# Revit family: 70740X0
name_source: partatom
category: Plumbing Fixtures
revit_build: Autodesk Revit 2018 (Build: 20170223_1515(x64)
units: mm (PartAtom-declared; Revit-internal decimal feet)

## family parameters
Always vertical = No
Cut with Voids When Loaded = No
OmniClass Number = 23.45.55.14
OmniClass Title = Single Faucets
Part Type = Normal
Room Calculation Point = No
Round Connector Dimension = Use Diameter
Shared = Yes
Work Plane-Based = Yes

## types (6) — shared parameters
ADA Compliant = Yes
Assembly Code = D2020300
CEC Compliant = Yes
CW Connection = No
CWFU = 1.5
CalGreen Compliant = Yes
Default Elevation = 0"
Flow Rate = 1.5 GPM (5.7L/min)
HW Connection = No
HWFU = 1.5
Height = 6 1/2"
Installation Type = Deck Mounted
Length = 10 3/8"
Length 2 = 9 1/8"
Manufacturer = American Standard
Product Documentation Link = https://americanstandard.box.com
Product Page URL = https://www.americanstandard-us.com
Revised Date = 08/13/2022
Tempered Water Connection = Yes
Tempered Water Connection Diameter = 3/8"
URL = http://www.americanstandard-us.com
Vent Connection = No
Warranty Information = Limited lifetime warranty
Waste Connection = No
Width = 8 1/2"
zero-valued in all types: WFU

## per-type parameters (varying)
| type | Deck Plate | Description | Finish | Material | Mounting Height Faucet | Side-Spray | Width 2 |
| 7074000.002 | Yes | Colony® PRO Single-Handle Kitchen Faucet 1.5 gpm/5.7 L/min | Brass-American Standard-002-Polished Chrome | Brass-American Standard-002-Polished Chrome | 3/8" | Yes | 8" |
| 7074010.002 | No | Colony® PRO Single-Handle Kitchen Faucet 1.5 gpm/5.7 L/min | Brass-American Standard-002-Polished Chrome | Brass-American Standard-002-Polished Chrome | 0" | No | 8" |
| 7074030.002 | Yes | Colony® PRO Single-Handle Kitchen Faucet 1.5 gpm/5.7 L/min With Side Spray | Brass-American Standard-002-Polished Chrome | Brass-American Standard-002-Polished Chrome | 3/8" | Yes | 3" |
| 7074040.002 | Yes | Colony® PRO Single-Handle Kitchen Faucet 1.5 gpm/5.7 L/min With Side Spray | Brass-American Standard-002-Polished Chrome | Brass-American Standard-002-Polished Chrome | 3/8" | Yes | 8" |
| 7074000.075 | Yes | Colony® PRO Single-Handle Kitchen Faucet 1.5 gpm/5.7 L/min | Brass-American Standard-075-Stainless Steel | Brass-American Standard-075-Stainless Steel | 3/8" | Yes | 8" |
| 7074040.075 | Yes | Colony® PRO Single-Handle Kitchen Faucet 1.5 gpm/5.7 L/min With Side Spray | Brass-American Standard-075-Stainless Steel | Brass-American Standard-075-Stainless Steel | 3/8" | Yes | 8" |

note: column(s) folded — value = type name in every type: Model

## geometry (parser evidence)
native form markers: Sweep x6
no freeform markers — native parametric forms only
